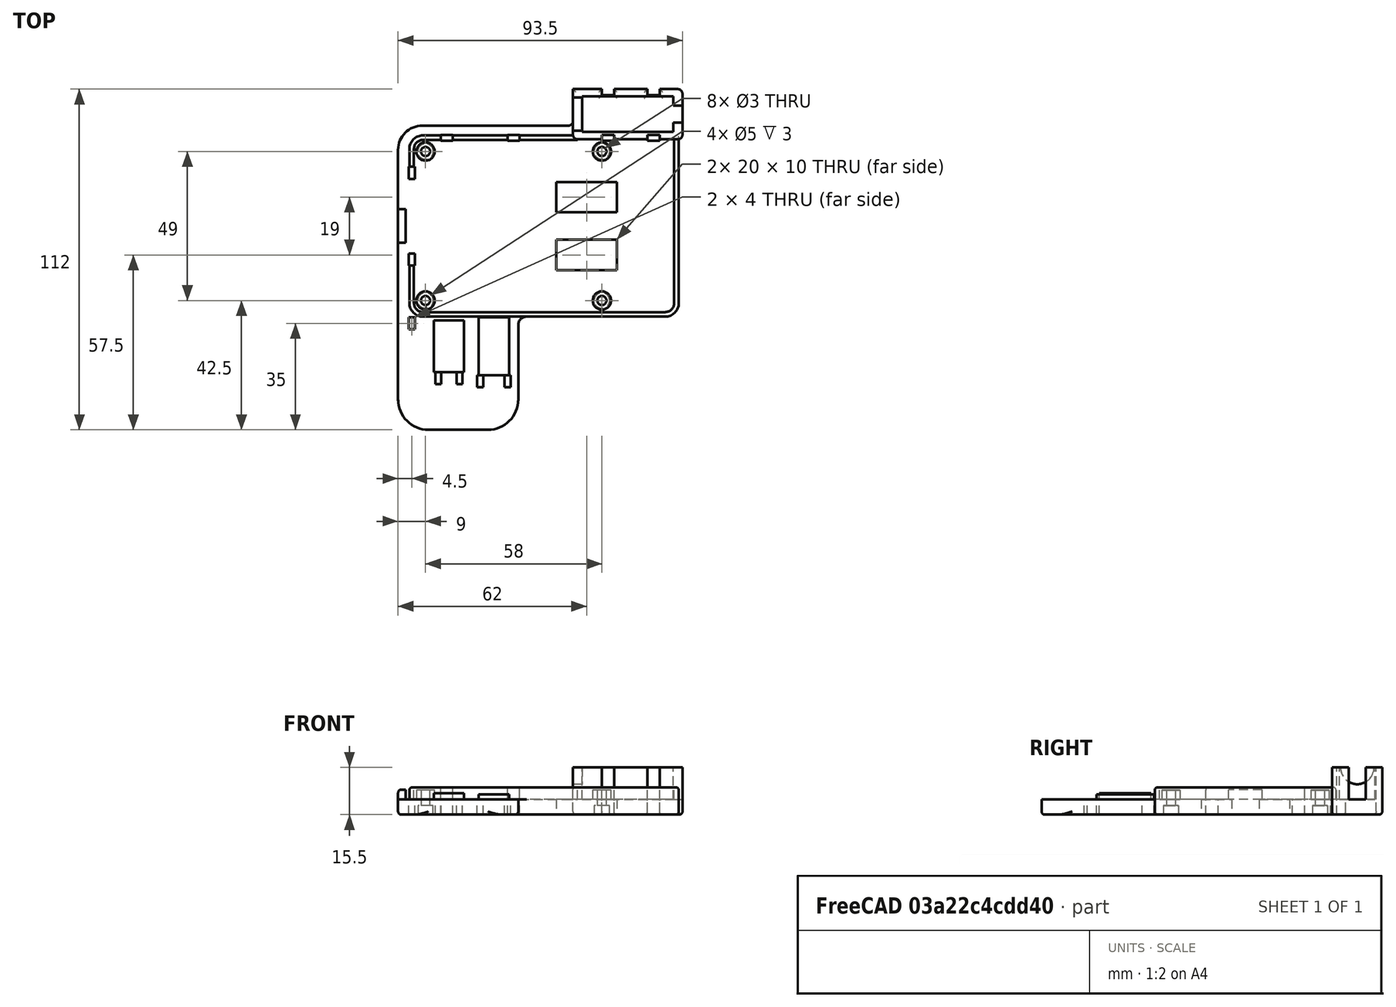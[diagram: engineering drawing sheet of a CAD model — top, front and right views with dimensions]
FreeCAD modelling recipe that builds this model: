
FCSTD DOCUMENT  (FreeCAD 0.18R4 (GitTag))
Label: v1.1raspberry_holster
License: All rights reserved
LicenseURL: http://en.wikipedia.org/wiki/All_rights_reserved
objects: Sketcher::SketchObject×12, PartDesign::Pad×7, PartDesign::Pocket×5, PartDesign::Fillet×3, Mesh::Feature×1, PartDesign::Body×1
note: 40 computed .brp shape members not serialized (recipe doc carries the construction recipe); baked Part::Feature solids carry a one-line shape summary decoded from their .brp

FEATURE [Mesh::Feature] Raspberry_Pi_4
  Placement = pos=(39,24.5,7.5) rot=(0,0,1;0rad)
FEATURE [Sketcher::SketchObject] Sketch  label="bottom_plane"
  MapMode = 5
  Support = -> [XY_Plane]
  sketch-geometry (71):
    g0: Circle CenterX=0 CenterY=49 CenterZ=0 NormalX=0 NormalY=0 NormalZ=1 AngleXU=0 Radius=1.5
    g1: Circle CenterX=58 CenterY=49 CenterZ=0 NormalX=0 NormalY=0 NormalZ=1 AngleXU=0 Radius=1.5
    g2: Circle CenterX=0 CenterY=0 CenterZ=0 NormalX=0 NormalY=0 NormalZ=1 AngleXU=0 Radius=1.5
    g3: Circle CenterX=58 CenterY=0 CenterZ=0 NormalX=0 NormalY=0 NormalZ=1 AngleXU=0 Radius=1.5
    g4: LineSegment StartX=84.5 StartY=68 StartZ=0 EndX=84.5 EndY=-5 EndZ=0
    g5: ArcOfCircle CenterX=83 CenterY=68 CenterZ=0 NormalX=0 NormalY=0 NormalZ=1 AngleXU=0 Radius=1.5 StartAngle=-9e-16 EndAngle=1.5708
    g6: LineSegment StartX=48.5 StartY=69.5 StartZ=0 EndX=48.5 EndY=59 EndZ=0
    g7: ArcOfCircle CenterX=47 CenterY=59 CenterZ=0 NormalX=0 NormalY=0 NormalZ=1 AngleXU=0 Radius=1.5 StartAngle=4.71239 EndAngle=6.28319
    g8: LineSegment StartX=47 StartY=57.5 StartZ=0 EndX=-1 EndY=57.5 EndZ=0
    g9: LineSegment StartX=-9 StartY=49.5 StartZ=0 EndX=-9 EndY=-41 EndZ=0
    g10: ArcOfCircle CenterX=-1 CenterY=49.5 CenterZ=0 NormalX=0 NormalY=0 NormalZ=1 AngleXU=0 Radius=8 StartAngle=1.5708 EndAngle=3.14159
    g11: LineSegment StartX=-7.5 StartY=-42.5 StartZ=0 EndX=29 EndY=-42.5 EndZ=0
    g12: ArcOfCircle CenterX=-7.5 CenterY=-41 CenterZ=0 NormalX=0 NormalY=0 NormalZ=1 AngleXU=0 Radius=1.5 StartAngle=3.14159 EndAngle=4.71239
    g13: ArcOfCircle CenterX=83 CenterY=-5 CenterZ=0 NormalX=0 NormalY=0 NormalZ=1 AngleXU=0 Radius=1.5 StartAngle=4.71239 EndAngle=6.28319
    g14: LineSegment StartX=32 StartY=-6.5 StartZ=0 EndX=83 EndY=-6.5 EndZ=0
    g15: LineSegment StartX=30.5 StartY=-8 StartZ=0 EndX=30.5 EndY=-41 EndZ=0
    g16: ArcOfCircle CenterX=32 CenterY=-8 CenterZ=0 NormalX=0 NormalY=0 NormalZ=1 AngleXU=0 Radius=1.5 StartAngle=1.5708 EndAngle=3.14159
    g17: ArcOfCircle CenterX=29 CenterY=-41 CenterZ=0 NormalX=0 NormalY=0 NormalZ=1 AngleXU=0 Radius=1.5 StartAngle=4.71239 EndAngle=6.28319
    g18: LineSegment StartX=58 StartY=52.5 StartZ=0 EndX=62 EndY=52.5 EndZ=0
    g19: LineSegment StartX=62 StartY=52.5 StartZ=0 EndX=62 EndY=54.5 EndZ=0
    g20: LineSegment StartX=62 StartY=54.5 StartZ=0 EndX=58 EndY=54.5 EndZ=0
    g21: LineSegment StartX=58 StartY=54.5 StartZ=0 EndX=58 EndY=52.5 EndZ=0
    g22: LineSegment StartX=73 StartY=54.5 StartZ=0 EndX=77 EndY=54.5 EndZ=0
    g23: LineSegment StartX=77 StartY=54.5 StartZ=0 EndX=77 EndY=52.5 EndZ=0
    g24: LineSegment StartX=77 StartY=52.5 StartZ=0 EndX=73 EndY=52.5 EndZ=0
    g25: LineSegment StartX=73 StartY=52.5 StartZ=0 EndX=73 EndY=54.5 EndZ=0
    g26: LineSegment StartX=48.5 StartY=69.5 StartZ=0 EndX=58 EndY=69.5 EndZ=0
    g27: LineSegment StartX=58 StartY=69.5 StartZ=0 EndX=58 EndY=67.5 EndZ=0
    g28: LineSegment StartX=58 StartY=67.5 StartZ=0 EndX=62 EndY=67.5 EndZ=0
    g29: LineSegment StartX=62 StartY=67.5 StartZ=0 EndX=62 EndY=69.5 EndZ=0
    g30: LineSegment StartX=62 StartY=69.5 StartZ=0 EndX=73 EndY=69.5 EndZ=0
    g31: LineSegment StartX=73 StartY=69.5 StartZ=0 EndX=73 EndY=67.5 EndZ=0
    g32: LineSegment StartX=73 StartY=67.5 StartZ=0 EndX=77 EndY=67.5 EndZ=0
    g33: LineSegment StartX=77 StartY=67.5 StartZ=0 EndX=77 EndY=69.5 EndZ=0
    g34: LineSegment StartX=77 StartY=69.5 StartZ=0 EndX=83 EndY=69.5 EndZ=0
    g35: LineSegment StartX=31 StartY=54.5 StartZ=0 EndX=27 EndY=54.5 EndZ=0
    g36: LineSegment StartX=27 StartY=54.5 StartZ=0 EndX=27 EndY=52.5 EndZ=0
    g37: LineSegment StartX=27 StartY=52.5 StartZ=0 EndX=31 EndY=52.5 EndZ=0
    g38: LineSegment StartX=31 StartY=52.5 StartZ=0 EndX=31 EndY=54.5 EndZ=0
    g39: LineSegment StartX=9 StartY=54.5 StartZ=0 EndX=5 EndY=54.5 EndZ=0
    g40: LineSegment StartX=5 StartY=54.5 StartZ=0 EndX=5 EndY=52.5 EndZ=0
    g41: LineSegment StartX=5 StartY=52.5 StartZ=0 EndX=9 EndY=52.5 EndZ=0
    g42: LineSegment StartX=9 StartY=52.5 StartZ=0 EndX=9 EndY=54.5 EndZ=0
    g43: LineSegment StartX=-5.5 StartY=44 StartZ=0 EndX=-3.5 EndY=44 EndZ=0
    g44: LineSegment StartX=-3.5 StartY=44 StartZ=0 EndX=-3.5 EndY=40 EndZ=0
    g45: LineSegment StartX=-3.5 StartY=40 StartZ=0 EndX=-5.5 EndY=40 EndZ=0
    g46: LineSegment StartX=-5.5 StartY=40 StartZ=0 EndX=-5.5 EndY=44 EndZ=0
    g47: LineSegment StartX=-5.5 StartY=15.5 StartZ=0 EndX=-3.5 EndY=15.5 EndZ=0
    g48: LineSegment StartX=-3.5 StartY=15.5 StartZ=0 EndX=-3.5 EndY=11.5 EndZ=0
    g49: LineSegment StartX=-3.5 StartY=11.5 StartZ=0 EndX=-5.5 EndY=11.5 EndZ=0
    g50: LineSegment StartX=-5.5 StartY=11.5 StartZ=0 EndX=-5.5 EndY=15.5 EndZ=0
    g51: LineSegment StartX=-5.5 StartY=-5.5 StartZ=0 EndX=-3.5 EndY=-5.5 EndZ=0
    g52: LineSegment StartX=-3.5 StartY=-5.5 StartZ=0 EndX=-3.5 EndY=-9.5 EndZ=0
    g53: LineSegment StartX=-3.5 StartY=-9.5 StartZ=0 EndX=-5.5 EndY=-9.5 EndZ=0
    g54: LineSegment StartX=-5.5 StartY=-9.5 StartZ=0 EndX=-5.5 EndY=-5.5 EndZ=0
    g55: LineSegment StartX=3.2 StartY=-23.5 StartZ=0 EndX=5.2 EndY=-23.5 EndZ=0
    g56: LineSegment StartX=5.2 StartY=-23.5 StartZ=0 EndX=5.2 EndY=-27.5 EndZ=0
    g57: LineSegment StartX=5.2 StartY=-27.5 StartZ=0 EndX=3.2 EndY=-27.5 EndZ=0
    g58: LineSegment StartX=3.2 StartY=-27.5 StartZ=0 EndX=3.2 EndY=-23.5 EndZ=0
    g59: LineSegment StartX=10.2 StartY=-23.5 StartZ=0 EndX=12.2 EndY=-23.5 EndZ=0
    g60: LineSegment StartX=12.2 StartY=-23.5 StartZ=0 EndX=12.2 EndY=-27.5 EndZ=0
    g61: LineSegment StartX=12.2 StartY=-27.5 StartZ=0 EndX=10.2 EndY=-27.5 EndZ=0
    g62: LineSegment StartX=10.2 StartY=-27.5 StartZ=0 EndX=10.2 EndY=-23.5 EndZ=0
    g63: LineSegment StartX=17 StartY=-24.5 StartZ=0 EndX=19 EndY=-24.5 EndZ=0
    g64: LineSegment StartX=19 StartY=-24.5 StartZ=0 EndX=19 EndY=-28.5 EndZ=0
    g65: LineSegment StartX=19 StartY=-28.5 StartZ=0 EndX=17 EndY=-28.5 EndZ=0
    g66: LineSegment StartX=17 StartY=-28.5 StartZ=0 EndX=17 EndY=-24.5 EndZ=0
    g67: LineSegment StartX=26 StartY=-24.5 StartZ=0 EndX=28 EndY=-24.5 EndZ=0
    g68: LineSegment StartX=28 StartY=-24.5 StartZ=0 EndX=28 EndY=-28.5 EndZ=0
    g69: LineSegment StartX=28 StartY=-28.5 StartZ=0 EndX=26 EndY=-28.5 EndZ=0
    g70: LineSegment StartX=26 StartY=-28.5 StartZ=0 EndX=26 EndY=-24.5 EndZ=0
  constraints (219):
    c: Coincident(g-1,g2)
    c: Vertical(g2,g0)
    c: Vertical(g1,g3)
    c: Horizontal(g1,g0)
    c: Horizontal(g3,g2)
    c: DistanceY(g2,g0) = 49
    c: DistanceX(g2,g3) = 58
    c: Radius(g2) = 1.5
    c: Equal(g2,g3)
    c: Equal(g3,g1)
    c: Equal(g1,g0)
    c: Vertical(g4)
    c: DistanceX(g3,g4) = 26.5
    c: Coincident(g5,g4)
    c: Vertical(g5,g5)
    c: Horizontal(g4,g5)
    c: Radius(g5) = 1.5
    c: Coincident(g6,g7)
    c: Vertical(g7,g7)
    c: Horizontal(g7,g6)
    c: Radius(g7) = 1.5
    c: Vertical(g6)
    c: DistanceX(g6,g4) = 36
    c: Coincident(g8,g7)
    c: Horizontal(g8)
    c: Vertical(g9)
    c: DistanceX(g9,g0) = 9
    c: DistanceY(g1,g7) = 8.5
    c: Coincident(g10,g8)
    c: Coincident(g9,g10)
    c: Vertical(g10,g8)
    c: Horizontal(g10,g9)
    c: Horizontal(g11)
    c: DistanceY(g11,g2) = 42.5
    c: Coincident(g11,g12)
    c: Coincident(g12,g9)
    c: Vertical(g12,g11)
    c: Horizontal(g9,g12)
    c: Radius(g12) = 1.5
    c: Coincident(g13,g4)
    c: Horizontal(g13,g4)
    c: Vertical(g13,g13)
    c: Radius(g13) = 1.5
    c: Coincident(g14,g13)
    c: Horizontal(g14)
    c: Coincident(g16,g14)
    c: Coincident(g16,g15)
    c: Vertical(g16,g14)
    c: Horizontal(g16,g15)
    c: DistanceY(g14,g3) = 6.5
    c: DistanceX(g2,g15) = 30.5
    c: Vertical(g15)
    c: Coincident(g17,g11)
    c: Coincident(g17,g15)
    c: Horizontal(g17,g15)
    c: Vertical(g11,g17)
    c: Radius(g17) = 1.5
    c: Radius(g16) = 1.5
    c: Coincident(g18,g19)
    c: Coincident(g19,g20)
    c: Coincident(g20,g21)
    c: Coincident(g21,g18)
    c: Horizontal(g18)
    c: Horizontal(g20)
    c: Vertical(g19)
    c: Vertical(g21)
    c: DistanceY(g18,g20) = 2
    c: DistanceX(g20,g19) = 4
    c: DistanceY(g1,g18) = 3.5
    c: Vertical(g1,g18)
    c: Coincident(g22,g23)
    c: Coincident(g23,g24)
    c: Coincident(g24,g25)
    c: Coincident(g25,g22)
    c: Horizontal(g22)
    c: Horizontal(g24)
    c: Vertical(g23)
    c: Vertical(g25)
    c: Horizontal(g22,g19)
    c: Horizontal(g24,g18)
    c: DistanceX(g22,g22) = 4
    c: DistanceX(g18,g24) = 15
    c: Coincident(g26,g27)
    c: Coincident(g27,g28)
    c: Coincident(g28,g29)
    c: Coincident(g29,g30)
    c: Coincident(g30,g31)
    c: Coincident(g31,g32)
    c: Coincident(g32,g33)
    c: Coincident(g33,g34)
    c: Coincident(g26,g6)
    c: Coincident(g34,g5)
    c: DistanceY(g1,g6) = 20.5
    c: Horizontal(g26)
    c: Horizontal(g30)
    c: Horizontal(g32)
    c: Horizontal(g34)
    c: Horizontal(g28)
    c: Vertical(g27)
    c: Vertical(g29)
    c: Vertical(g31)
    c: Vertical(g33)
    c: Horizontal(g26,g29)
    c: Horizontal(g30,g33)
    c: Horizontal(g31,g28)
    c: Vertical(g28,g19)
    c: Vertical(g20,g27)
    c: Vertical(g22,g31)
    c: Vertical(g22,g32)
    c: DistanceY(g28,g29) = 2
    c: Coincident(g35,g36)
    c: Coincident(g36,g37)
    c: Coincident(g38,g35)
    c: Horizontal(g35)
    c: Horizontal(g37)
    c: Vertical(g36)
    c: Vertical(g38)
    c: Coincident(g39,g40)
    c: Coincident(g40,g41)
    c: Coincident(g41,g42)
    c: Coincident(g42,g39)
    c: Horizontal(g39)
    c: Horizontal(g41)
    c: Vertical(g40)
    c: Vertical(g42)
    c: Coincident(g43,g44)
    c: Coincident(g44,g45)
    c: Coincident(g45,g46)
    c: Coincident(g46,g43)
    c: Horizontal(g43)
    c: Horizontal(g45)
    c: Vertical(g44)
    c: Vertical(g46)
    c: Coincident(g47,g48)
    c: Coincident(g48,g49)
    c: Coincident(g49,g50)
    c: Coincident(g50,g47)
    c: Horizontal(g47)
    c: Horizontal(g49)
    c: Vertical(g48)
    c: Vertical(g50)
    c: DistanceY(g1,g37) = 3.5
    c: DistanceX(g36,g37) = 4
    c: DistanceY(g37,g35) = 2
    c: DistanceX(g40,g41) = 4
    c: Horizontal(g41,g36)
    c: Horizontal(g39,g35)
    c: DistanceX(g37,g1) = 27
    c: DistanceX(g43,g0) = 3.5
    c: DistanceX(g43,g43) = 2
    c: DistanceY(g44,g43) = 4
    c: Vertical(g44,g47)
    c: Vertical(g47,g45)
    c: DistanceY(g49,g47) = 4
    c: DistanceY(g43,g0) = 5
    c: DistanceX(g0,g40) = 5
    c: DistanceY(g47,g44) = 24.5
    c: Coincident(g37,g38)
    c: Coincident(g51,g52)
    c: Coincident(g52,g53)
    c: Coincident(g53,g54)
    c: Coincident(g54,g51)
    c: Horizontal(g51)
    c: Horizontal(g53)
    c: Vertical(g52)
    c: Vertical(g54)
    c: Vertical(g51,g49)
    c: Vertical(g51,g48)
    c: DistanceY(g53,g51) = 4
    c: DistanceY(g51,g48) = 17
    c: Coincident(g55,g56)
    c: Coincident(g56,g57)
    c: Coincident(g57,g58)
    c: Coincident(g58,g55)
    c: Horizontal(g55)
    c: Horizontal(g57)
    c: Vertical(g56)
    c: Vertical(g58)
    c: Coincident(g59,g60)
    c: Coincident(g60,g61)
    c: Coincident(g61,g62)
    c: Coincident(g62,g59)
    c: Horizontal(g59)
    c: Horizontal(g61)
    c: Vertical(g60)
    c: Vertical(g62)
    c: Coincident(g63,g64)
    c: Coincident(g64,g65)
    c: Coincident(g65,g66)
    c: Coincident(g66,g63)
    c: Horizontal(g63)
    c: Horizontal(g65)
    c: Vertical(g64)
    c: Vertical(g66)
    c: Coincident(g67,g68)
    c: Coincident(g68,g69)
    c: Coincident(g69,g70)
    c: Coincident(g70,g67)
    c: Horizontal(g67)
    c: Horizontal(g69)
    c: Vertical(g68)
    c: Vertical(g70)
    c: DistanceX(g55,g55) = 2
    c: DistanceY(g56,g55) = 4
    c: Horizontal(g56,g61)
    c: Horizontal(g65,g69)
    c: Horizontal(g67,g63)
    c: Horizontal(g59,g55)
    c: DistanceX(g59,g59) = 2
    c: DistanceX(g63,g63) = 2
    c: DistanceX(g67,g67) = 2
    c: DistanceX(g56,g61) = 5
    c: DistanceX(g64,g69) = 7
    c: DistanceY(g65,g63) = 4
    c: DistanceY(g55,g2) = 23.5
    c: DistanceY(g63,g2) = 24.5
    c: DistanceX(g2,g55) = 5.2
    c: DistanceX(g2,g63) = 19
    c: Radius(g10) = 8
FEATURE [PartDesign::Pad] Pad  label="bottom_plane_pad"
  Length = 5
  Length2 = 100
  Profile = -> Sketch
  Type = 0
FEATURE [Sketcher::SketchObject] Sketch001  label="standoffs"
  ExternalGeometry = -> [Pad]
  MapMode = 5
  Placement = pos=(0,0,5) rot=(0,0,1;0rad)
  Support = -> [Pad]
  sketch-geometry (8):
    g0: Circle CenterX=0 CenterY=49 CenterZ=0 NormalX=0 NormalY=0 NormalZ=1 AngleXU=0 Radius=3
    g1: Circle CenterX=58 CenterY=49 CenterZ=0 NormalX=0 NormalY=0 NormalZ=1 AngleXU=0 Radius=3
    g2: Circle CenterX=58 CenterY=0 CenterZ=0 NormalX=0 NormalY=0 NormalZ=1 AngleXU=0 Radius=3
    g3: Circle CenterX=0 CenterY=0 CenterZ=0 NormalX=0 NormalY=0 NormalZ=1 AngleXU=0 Radius=3
    g4: Circle CenterX=58 CenterY=0 CenterZ=0 NormalX=0 NormalY=0 NormalZ=1 AngleXU=0 Radius=1.5
    g5: Circle CenterX=58 CenterY=49 CenterZ=0 NormalX=0 NormalY=0 NormalZ=1 AngleXU=0 Radius=1.5
    g6: Circle CenterX=0 CenterY=49 CenterZ=0 NormalX=0 NormalY=0 NormalZ=1 AngleXU=0 Radius=1.5
    g7: Circle CenterX=0 CenterY=0 CenterZ=0 NormalX=0 NormalY=0 NormalZ=1 AngleXU=0 Radius=1.5
  constraints (16):
    c: Coincident(g3,g-1)
    c: Coincident(g-5,g0)
    c: Coincident(g-6,g1)
    c: Coincident(g-3,g2)
    c: Equal(g2,g1)
    c: Equal(g1,g0)
    c: Equal(g0,g3)
    c: Radius(g1) = 3
    c: Coincident(g7,g3)
    c: Coincident(g2,g4)
    c: Coincident(g5,g1)
    c: Coincident(g6,g0)
    c: Equal(g5,g4)
    c: Equal(g4,g7)
    c: Equal(g7,g6)
    c: Equal(g6,g-5)
FEATURE [PartDesign::Pad] Pad001  label="standoffs_pad"
  BaseFeature = -> Pad
  Length = 3
  Length2 = 100
  Profile = -> Sketch001
  Type = 0
FEATURE [Sketcher::SketchObject] Sketch002  label="HDMI_holder"
  ExternalGeometry = -> [Pad001]
  MapMode = 5
  Placement = pos=(0,0,5) rot=(0,0,1;0rad)
  Support = -> [Pad001]
  sketch-geometry (31):
    g0: LineSegment StartX=84.5 StartY=54.5 StartZ=0 EndX=84.5 EndY=58.5 EndZ=0
    g1: LineSegment StartX=51.5 StartY=55.5 StartZ=0 EndX=81.5 EndY=55.5 EndZ=0
    g2: LineSegment StartX=81.5 StartY=55.5 StartZ=0 EndX=81.5 EndY=58.5 EndZ=0
    g3: LineSegment StartX=81.5 StartY=58.5 StartZ=0 EndX=84.5 EndY=58.5 EndZ=0
    g4: LineSegment StartX=51.5 StartY=55.5 StartZ=0 EndX=51.5 EndY=67.1 EndZ=0
    g5: LineSegment StartX=48.5 StartY=69.5 StartZ=0 EndX=48.5 EndY=54.5 EndZ=0
    g6: LineSegment StartX=51.5 StartY=67.1 StartZ=0 EndX=81.5 EndY=67.1 EndZ=0
    g7: LineSegment StartX=81.5 StartY=67.1 StartZ=0 EndX=81.5 EndY=64.1 EndZ=0
    g8: LineSegment StartX=81.5 StartY=64.1 StartZ=0 EndX=84.5 EndY=64.1 EndZ=0
    g9: LineSegment StartX=84.5 StartY=64.1 StartZ=0 EndX=84.5 EndY=68 EndZ=0
    g10: ArcOfCircle CenterX=83 CenterY=68 CenterZ=0 NormalX=0 NormalY=0 NormalZ=1 AngleXU=0 Radius=1.5 StartAngle=1.4e-15 EndAngle=1.5708
    g11: LineSegment StartX=83 StartY=69.5 StartZ=0 EndX=77 EndY=69.5 EndZ=0
    g12: LineSegment StartX=77 StartY=69.5 StartZ=0 EndX=77 EndY=67.5 EndZ=0
    g13: LineSegment StartX=77 StartY=67.5 StartZ=0 EndX=73 EndY=67.5 EndZ=0
    g14: LineSegment StartX=73 StartY=67.5 StartZ=0 EndX=73 EndY=69.5 EndZ=0
    g15: LineSegment StartX=73 StartY=69.5 StartZ=0 EndX=62 EndY=69.5 EndZ=0
    g16: LineSegment StartX=62 StartY=69.5 StartZ=0 EndX=62 EndY=67.5 EndZ=0
    g17: LineSegment StartX=62 StartY=67.5 StartZ=0 EndX=58 EndY=67.5 EndZ=0
    g18: LineSegment StartX=58 StartY=67.5 StartZ=0 EndX=58 EndY=69.5 EndZ=0
    g19: LineSegment StartX=58 StartY=69.5 StartZ=0 EndX=48.5 EndY=69.5 EndZ=0
    g20: ArcOfCircle CenterX=50 CenterY=54.5 CenterZ=0 NormalX=0 NormalY=0 NormalZ=1 AngleXU=0 Radius=1.5 StartAngle=3.14159 EndAngle=4.71239
    g21: LineSegment StartX=83 StartY=53 StartZ=0 EndX=77 EndY=53 EndZ=0
    g22: LineSegment StartX=77 StartY=53 StartZ=0 EndX=77 EndY=54.5 EndZ=0
    g23: LineSegment StartX=77 StartY=54.5 StartZ=0 EndX=73 EndY=54.5 EndZ=0
    g24: LineSegment StartX=73 StartY=54.5 StartZ=0 EndX=73 EndY=53 EndZ=0
    g25: LineSegment StartX=73 StartY=53 StartZ=0 EndX=62 EndY=53 EndZ=0
    g26: LineSegment StartX=62 StartY=53 StartZ=0 EndX=62 EndY=54.5 EndZ=0
    g27: LineSegment StartX=62 StartY=54.5 StartZ=0 EndX=58 EndY=54.5 EndZ=0
    g28: LineSegment StartX=58 StartY=54.5 StartZ=0 EndX=58 EndY=53 EndZ=0
    g29: LineSegment StartX=58 StartY=53 StartZ=0 EndX=50 EndY=53 EndZ=0
    g30: ArcOfCircle CenterX=83 CenterY=54.5 CenterZ=0 NormalX=0 NormalY=0 NormalZ=1 AngleXU=0 Radius=1.5 StartAngle=4.71239 EndAngle=6.28319
  constraints (84):
    c: Vertical(g0,g-6)
    c: Horizontal(g1)
    c: DistanceY(g20,g1) = 2.5
    c: Coincident(g0,g3)
    c: Coincident(g3,g2)
    c: Coincident(g2,g1)
    c: DistanceX(g2,g0) = 3
    c: Vertical(g0)
    c: Horizontal(g3)
    c: Vertical(g2)
    c: DistanceX(g1,g1) = 30
    c: DistanceY(g1,g2) = 3
    c: Coincident(g4,g6)
    c: Coincident(g1,g4)
    c: Coincident(g8,g9)
    c: Coincident(g7,g8)
    c: Coincident(g6,g7)
    c: Horizontal(g6)
    c: Vertical(g4)
    c: DistanceY(g1,g4) = 11.6
    c: Vertical(g7)
    c: Horizontal(g8)
    c: Vertical(g9)
    c: Vertical(g7,g2)
    c: DistanceY(g7,g6) = 3
    c: Coincident(g9,g-6)
    c: Coincident(g9,g10)
    c: Horizontal(g9,g10)
    c: Vertical(g10,g10)
    c: Radius(g10) = 1.5
    c: Coincident(g11,g12)
    c: Coincident(g12,g13)
    c: Coincident(g13,g14)
    c: Coincident(g14,g15)
    c: Coincident(g15,g16)
    c: Coincident(g16,g17)
    c: Coincident(g17,g18)
    c: Coincident(g18,g19)
    c: Coincident(g11,g10)
    c: Horizontal(g11)
    c: Vertical(g12)
    c: Coincident(g12,g-4)
    c: Coincident(g13,g-4)
    c: Coincident(g14,g-7)
    c: Coincident(g15,g-7)
    c: Coincident(g16,g-5)
    c: Coincident(g17,g-5)
    c: Coincident(g19,g-8)
    c: Horizontal(g19)
    c: Vertical(g18)
    c: Coincident(g5,g19)
    c: Coincident(g5,g20)
    c: Horizontal(g20,g5)
    c: Vertical(g20,g20)
    c: Radius(g20) = 1.5
    c: Vertical(g5)
    c: Coincident(g21,g22)
    c: Coincident(g22,g23)
    c: Coincident(g23,g24)
    c: Coincident(g24,g25)
    c: Coincident(g25,g26)
    c: Coincident(g26,g27)
    c: Coincident(g27,g28)
    c: Coincident(g28,g29)
    c: Coincident(g20,g29)
    c: Coincident(g27,g-12)
    c: Coincident(g26,g-11)
    c: Coincident(g23,g-10)
    c: Coincident(g22,g-9)
    c: Coincident(g30,g0)
    c: Coincident(g21,g30)
    c: Vertical(g30,g21)
    c: Horizontal(g30,g0)
    c: Radius(g30) = 1.5
    c: DistanceY(g-3,g28) = 4
    c: Horizontal(g29)
    c: Horizontal(g25)
    c: Horizontal(g21)
    c: Horizontal(g21,g24)
    c: Horizontal(g25,g28)
    c: Vertical(g28)
    c: Vertical(g26)
    c: Vertical(g24)
    c: Vertical(g22)
FEATURE [PartDesign::Pad] Pad002  label="HDMI_holder_pad"
  BaseFeature = -> Pad001
  Length = 10.5
  Length2 = 100
  Profile = -> Sketch002
  Type = 0
FEATURE [Sketcher::SketchObject] Sketch003  label="HDMI_wire_hole"
  ExternalGeometry = -> [Pad002]
  MapMode = 5
  Placement = pos=(48.5,0,0) rot=(0.57735,-0.57735,-0.57735;2.0944rad)
  Support = -> [Pad002]
  sketch-geometry (1):
    g0: Circle CenterX=-61.3 CenterY=15.5 CenterZ=0 NormalX=0 NormalY=0 NormalZ=1 AngleXU=0 Radius=5.5
  constraints (1):
    c: Radius(g0) = 5.5
FEATURE [PartDesign::Pocket] Pocket  label="Pocket_HDMI_wire_hole"
  BaseFeature = -> Pad002
  Length = 5
  Length2 = 100
  Profile = -> Sketch003
  Type = 0
FEATURE [Sketcher::SketchObject] Sketch004  label="SDcard_holder"
  ExternalGeometry = -> [Pocket]
  MapMode = 5
  Placement = pos=(0,0,5) rot=(0,0,1;0rad)
  Support = -> [Pocket]
  sketch-geometry (4):
    g0: LineSegment StartX=-9 StartY=30 StartZ=0 EndX=-6.5 EndY=30 EndZ=0
    g1: LineSegment StartX=-6.5 StartY=30 StartZ=0 EndX=-6.5 EndY=19 EndZ=0
    g2: LineSegment StartX=-6.5 StartY=19 StartZ=0 EndX=-9 EndY=19 EndZ=0
    g3: LineSegment StartX=-9 StartY=19 StartZ=0 EndX=-9 EndY=30 EndZ=0
  constraints (12):
    c: Coincident(g0,g1)
    c: Coincident(g1,g2)
    c: Coincident(g2,g3)
    c: Coincident(g3,g0)
    c: Horizontal(g0)
    c: Horizontal(g2)
    c: Vertical(g1)
    c: Vertical(g3)
    c: DistanceY(g-1,g1) = 19
    c: DistanceY(g0,g-4) = 19
    c: Vertical(g0,g-5)
    c: DistanceX(g1,g-1) = 6.5
FEATURE [PartDesign::Pad] Pad003  label="SDcard_holder_pad"
  BaseFeature = -> Pocket
  Length = 3.2
  Length2 = 100
  Profile = -> Sketch004
  Type = 0
FEATURE [Sketcher::SketchObject] Sketch005  label="typeC_support"
  ExternalGeometry = -> [Pad003]
  MapMode = 5
  Placement = pos=(0,0,5) rot=(0,0,1;0rad)
  Support = -> [Pad003]
  sketch-geometry (4):
    g0: LineSegment StartX=2.7 StartY=-6.5 StartZ=0 EndX=12.7 EndY=-6.5 EndZ=0
    g1: LineSegment StartX=12.7 StartY=-6.5 StartZ=0 EndX=12.7 EndY=-23.5 EndZ=0
    g2: LineSegment StartX=12.7 StartY=-23.5 StartZ=0 EndX=2.7 EndY=-23.5 EndZ=0
    g3: LineSegment StartX=2.7 StartY=-23.5 StartZ=0 EndX=2.7 EndY=-6.5 EndZ=0
  constraints (12):
    c: Coincident(g0,g1)
    c: Coincident(g1,g2)
    c: Coincident(g2,g3)
    c: Coincident(g3,g0)
    c: Horizontal(g0)
    c: Horizontal(g2)
    c: Vertical(g1)
    c: Vertical(g3)
    c: DistanceX(g0,g0) = 10
    c: DistanceY(g1,g1) = 17
    c: Horizontal(g2,g-4)
    c: DistanceX(g-1,g0) = 2.7
FEATURE [PartDesign::Pad] Pad004  label="typeC_support_pad"
  BaseFeature = -> Pad003
  Length = 2
  Length2 = 100
  Profile = -> Sketch005
  Type = 0
FEATURE [Sketcher::SketchObject] Sketch006  label="microHDMI_support"
  ExternalGeometry = -> [Pad004]
  MapMode = 5
  Placement = pos=(0,0,5) rot=(0,0,1;0rad)
  Support = -> [Pad004]
  sketch-geometry (4):
    g0: LineSegment StartX=17.5 StartY=-5.5 StartZ=0 EndX=27.5 EndY=-5.5 EndZ=0
    g1: LineSegment StartX=27.5 StartY=-5.5 StartZ=0 EndX=27.5 EndY=-24.5 EndZ=0
    g2: LineSegment StartX=27.5 StartY=-24.5 StartZ=0 EndX=17.5 EndY=-24.5 EndZ=0
    g3: LineSegment StartX=17.5 StartY=-24.5 StartZ=0 EndX=17.5 EndY=-5.5 EndZ=0
  constraints (12):
    c: Coincident(g0,g1)
    c: Coincident(g1,g2)
    c: Coincident(g2,g3)
    c: Coincident(g3,g0)
    c: Horizontal(g0)
    c: Horizontal(g2)
    c: Vertical(g1)
    c: Vertical(g3)
    c: DistanceX(g0,g0) = 10
    c: DistanceY(g1,g1) = 19
    c: Horizontal(g2,g-4)
    c: DistanceX(g-1,g0) = 17.5
FEATURE [PartDesign::Pad] Pad005  label="microHDMI_support_pad"
  BaseFeature = -> Pad004
  Length = 1.7
  Length2 = 100
  Profile = -> Sketch006
  Type = 0
FEATURE [Sketcher::SketchObject] Sketch007  label="dust_cover"
  ExternalGeometry = -> [Pad005]
  MapMode = 5
  Placement = pos=(0,0,5) rot=(0,0,1;0rad)
  Support = -> [Pad005]
  sketch-geometry (30):
    g0: LineSegment StartX=81.8 StartY=53 StartZ=0 EndX=81.8 EndY=-0.8 EndZ=0
    g1: LineSegment StartX=78.8 StartY=-3.8 StartZ=0 EndX=-0.8 EndY=-3.8 EndZ=0
    g2: LineSegment StartX=-3.8 StartY=49.8 StartZ=0 EndX=-3.8 EndY=44 EndZ=0
    g3: LineSegment StartX=-3.8 StartY=11.5 StartZ=0 EndX=-3.8 EndY=-0.8 EndZ=0
    g4: LineSegment StartX=-3.8 StartY=11.5 StartZ=0 EndX=-5.3 EndY=11.5 EndZ=0
    g5: ArcOfCircle CenterX=-0.8 CenterY=-0.8 CenterZ=0 NormalX=0 NormalY=0 NormalZ=1 AngleXU=0 Radius=3 StartAngle=3.14159 EndAngle=4.71239
    g6: ArcOfCircle CenterX=78.8 CenterY=-0.8 CenterZ=0 NormalX=0 NormalY=0 NormalZ=1 AngleXU=0 Radius=3 StartAngle=4.71239 EndAngle=6.28319
    g7: LineSegment StartX=81.8 StartY=53 StartZ=0 EndX=83 EndY=53 EndZ=0
    g8: LineSegment StartX=83.3 StartY=53.0303 StartZ=0 EndX=83.3 EndY=-0.8 EndZ=0
    g9: ArcOfCircle CenterX=83 CenterY=54.5 CenterZ=0 NormalX=0 NormalY=0 NormalZ=1 AngleXU=0 Radius=1.5 StartAngle=4.71239 EndAngle=4.91375
    g10: ArcOfCircle CenterX=78.8 CenterY=-0.8 CenterZ=0 NormalX=0 NormalY=0 NormalZ=1 AngleXU=0 Radius=4.5 StartAngle=4.71239 EndAngle=6.28319
    g11: LineSegment StartX=-0.8 StartY=-5.3 StartZ=0 EndX=78.8 EndY=-5.3 EndZ=0
    g12: ArcOfCircle CenterX=-0.8 CenterY=-0.8 CenterZ=0 NormalX=0 NormalY=0 NormalZ=1 AngleXU=0 Radius=4.5 StartAngle=3.14159 EndAngle=4.71239
    g13: LineSegment StartX=-5.3 StartY=-0.8 StartZ=0 EndX=-5.3 EndY=11.5 EndZ=0
    g14: LineSegment StartX=5 StartY=54.3 StartZ=0 EndX=5 EndY=52.8 EndZ=0
    g15: LineSegment StartX=5 StartY=54.3 StartZ=0 EndX=-0.8 EndY=54.3 EndZ=0
    g16: ArcOfCircle CenterX=-0.8 CenterY=49.8 CenterZ=0 NormalX=0 NormalY=0 NormalZ=1 AngleXU=0 Radius=4.5 StartAngle=1.5708 EndAngle=3.14159
    g17: LineSegment StartX=-3.8 StartY=44 StartZ=0 EndX=-5.3 EndY=44 EndZ=0
    g18: LineSegment StartX=-5.3 StartY=49.8 StartZ=0 EndX=-5.3 EndY=44 EndZ=0
    g19: LineSegment StartX=9 StartY=54.3 StartZ=0 EndX=27 EndY=54.3 EndZ=0
    g20: LineSegment StartX=27 StartY=54.3 StartZ=0 EndX=27 EndY=52.8 EndZ=0
    g21: LineSegment StartX=27 StartY=52.8 StartZ=0 EndX=9 EndY=52.8 EndZ=0
    g22: LineSegment StartX=9 StartY=52.8 StartZ=0 EndX=9 EndY=54.3 EndZ=0
    g23: LineSegment StartX=31 StartY=54.3 StartZ=0 EndX=31 EndY=52.8 EndZ=0
    g24: LineSegment StartX=31 StartY=52.8 StartZ=0 EndX=50 EndY=52.8 EndZ=0
    g25: LineSegment StartX=31 StartY=54.3 StartZ=0 EndX=48.5134 EndY=54.3 EndZ=0
    g26: LineSegment StartX=-0.8 StartY=52.8 StartZ=0 EndX=5 EndY=52.8 EndZ=0
    g27: LineSegment StartX=50 StartY=53 StartZ=0 EndX=50 EndY=52.8 EndZ=0
    g28: ArcOfCircle CenterX=50 CenterY=54.5 CenterZ=0 NormalX=0 NormalY=0 NormalZ=1 AngleXU=0 Radius=1.5 StartAngle=3.27532 EndAngle=4.71239
    g29: ArcOfCircle CenterX=-0.8 CenterY=49.8 CenterZ=0 NormalX=0 NormalY=0 NormalZ=1 AngleXU=0 Radius=3 StartAngle=1.5708 EndAngle=3.14159
  constraints (91):
    c: Vertical(g0)
    c: Horizontal(g1)
    c: Vertical(g3)
    c: Vertical(g2)
    c: DistanceX(g-3,g0) = 23.8
    c: DistanceY(g1,g-6) = 3.8
    c: Coincident(g4,g3)
    c: Horizontal(g3,g-7)
    c: Coincident(g5,g3)
    c: Coincident(g5,g1)
    c: Coincident(g6,g0)
    c: Coincident(g6,g1)
    c: Coincident(g7,g0)
    c: Horizontal(g7)
    c: Coincident(g7,g9)
    c: Coincident(g7,g-8)
    c: Vertical(g8)
    c: Coincident(g10,g8)
    c: Coincident(g10,g6)
    c: Coincident(g11,g10)
    c: Horizontal(g11)
    c: Coincident(g11,g12)
    c: Coincident(g12,g5)
    c: Coincident(g9,g-8)
    c: Coincident(g8,g9)
    c: DistanceX(g0,g8) = 1.5
    c: Coincident(g4,g13)
    c: Coincident(g12,g13)
    c: Vertical(g13)
    c: Horizontal(g4)
    c: Vertical(g14,g-9)
    c: Coincident(g14,g15)
    c: Vertical(g14)
    c: Horizontal(g15)
    c: Coincident(g15,g16)
    c: DistanceY(g26,g15) = 1.5
    c: Horizontal(g2,g-10)
    c: Coincident(g17,g2)
    c: Coincident(g17,g18)
    c: Coincident(g18,g16)
    c: Vertical(g18)
    c: Horizontal(g17)
    c: Coincident(g19,g20)
    c: Coincident(g20,g21)
    c: Coincident(g21,g22)
    c: Coincident(g22,g19)
    c: Horizontal(g19)
    c: Horizontal(g21)
    c: Vertical(g20)
    c: Vertical(g22)
    c: Vertical(g21,g-9)
    c: Vertical(g20,g-11)
    c: Horizontal(g21,g14)
    c: Horizontal(g19,g14)
    c: Coincident(g23,g24)
    c: Coincident(g23,g25)
    c: Vertical(g23)
    c: Vertical(g23,g-11)
    c: Horizontal(g23,g20)
    c: Horizontal(g23,g19)
    c: Horizontal(g24)
    c: Horizontal(g25)
    c: Coincident(g14,g26)
    c: Horizontal(g26)
    c: Coincident(g24,g27)
    c: Coincident(g27,g-12)
    c: Vertical(g27)
    c: Coincident(g25,g28)
    c: Coincident(g28,g27)
    c: Coincident(g28,g-12)
    c: Radius(g6) = 3
    c: Vertical(g10,g1)
    c: Vertical(g1,g6)
    c: Horizontal(g0,g6)
    c: Horizontal(g6,g8)
    c: Radius(g5) = 3
    c: Horizontal(g5,g3)
    c: Horizontal(g3,g12)
    c: Vertical(g11,g1)
    c: Vertical(g1,g5)
    c: DistanceX(g3,g-1) = 3.8
    c: Vertical(g26,g15)
    c: Horizontal(g2,g16)
    c: Coincident(g29,g26)
    c: Coincident(g29,g2)
    c: Coincident(g16,g29)
    c: Radius(g29) = 3
    c: Horizontal(g16,g2)
    c: Vertical(g16,g26)
    c: DistanceY(g-4,g26) = 3.8
    c: DistanceX(g2,g-4) = 3.8
FEATURE [PartDesign::Pad] Pad006  label="dust_cover_pad"
  BaseFeature = -> Pad005
  Length = 4
  Length2 = 100
  Profile = -> Sketch007
  Type = 0
FEATURE [Sketcher::SketchObject] Sketch008  label="top edge trim"
  ExternalGeometry = -> [Pad006]
  MapMode = 5
  Placement = pos=(0,0,5) rot=(0,0,1;0rad)
  Support = -> [Pad006]
  sketch-geometry (7):
    g0: ArcOfCircle CenterX=83 CenterY=54.5 CenterZ=0 NormalX=0 NormalY=0 NormalZ=1 AngleXU=0 Radius=1.5 StartAngle=4.91375 EndAngle=6.28319
    g1: LineSegment StartX=84.5 StartY=54.5 StartZ=0 EndX=84.5 EndY=-8 EndZ=0
    g2: LineSegment StartX=84.5 StartY=-8 StartZ=0 EndX=30.5 EndY=-8 EndZ=0
    g3: ArcOfCircle CenterX=33.2 CenterY=-8 CenterZ=0 NormalX=0 NormalY=0 NormalZ=1 AngleXU=0 Radius=2.7 StartAngle=1.5708 EndAngle=3.14159
    g4: LineSegment StartX=33.2 StartY=-5.3 StartZ=0 EndX=78.8 EndY=-5.3 EndZ=0
    g5: ArcOfCircle CenterX=78.8 CenterY=-0.8 CenterZ=0 NormalX=0 NormalY=0 NormalZ=1 AngleXU=0 Radius=4.5 StartAngle=4.71239 EndAngle=6.28319
    g6: LineSegment StartX=83.3 StartY=-0.8 StartZ=0 EndX=83.3 EndY=53.0303 EndZ=0
  constraints (19):
    c: Coincident(g0,g-7)
    c: Coincident(g0,g-3)
    c: Horizontal(g0,g0)
    c: Vertical(g1)
    c: Horizontal(g2)
    c: Coincident(g2,g1)
    c: Coincident(g1,g0)
    c: Coincident(g2,g-6)
    c: Coincident(g3,g2)
    c: Horizontal(g2,g3)
    c: Vertical(g3,g3)
    c: Horizontal(g3,g-5)
    c: Coincident(g4,g3)
    c: Coincident(g4,g-5)
    c: Coincident(g5,g4)
    c: Coincident(g5,g-4)
    c: Vertical(g4,g5)
    c: Coincident(g6,g5)
    c: Coincident(g6,g0)
FEATURE [PartDesign::Pocket] Pocket001  label="top edge trim pocket"
  BaseFeature = -> Pad006
  Length = 5
  Length2 = 100
  Profile = -> Sketch008
  Type = 0
FEATURE [Sketcher::SketchObject] Sketch009  label="belt clip guide"
  ExternalGeometry = -> [Pocket001]
  MapMode = 5
  Placement = pos=(0,0,5) rot=(0,0,1;0rad)
  Support = -> [Pocket001]
  sketch-geometry (8):
    g0: LineSegment StartX=63 StartY=39 StartZ=0 EndX=43 EndY=39 EndZ=0
    g1: LineSegment StartX=43 StartY=39 StartZ=0 EndX=43 EndY=29 EndZ=0
    g2: LineSegment StartX=43 StartY=29 StartZ=0 EndX=63 EndY=29 EndZ=0
    g3: LineSegment StartX=63 StartY=29 StartZ=0 EndX=63 EndY=39 EndZ=0
    g4: LineSegment StartX=63 StartY=20 StartZ=0 EndX=43 EndY=20 EndZ=0
    g5: LineSegment StartX=43 StartY=20 StartZ=0 EndX=43 EndY=10 EndZ=0
    g6: LineSegment StartX=43 StartY=10 StartZ=0 EndX=63 EndY=10 EndZ=0
    g7: LineSegment StartX=63 StartY=10 StartZ=0 EndX=63 EndY=20 EndZ=0
  constraints (24):
    c: Coincident(g0,g1)
    c: Coincident(g1,g2)
    c: Coincident(g2,g3)
    c: Coincident(g3,g0)
    c: Horizontal(g0)
    c: Horizontal(g2)
    c: Vertical(g1)
    c: Vertical(g3)
    c: Coincident(g4,g5)
    c: Coincident(g5,g6)
    c: Coincident(g6,g7)
    c: Coincident(g7,g4)
    c: Horizontal(g4)
    c: Horizontal(g6)
    c: Vertical(g5)
    c: Vertical(g7)
    c: Vertical(g4,g1)
    c: Vertical(g4,g2)
    c: DistanceY(g6,g4) = 10
    c: DistanceY(g2,g0) = 10
    c: DistanceX(g-3,g0) = 5
    c: DistanceX(g5,g6) = 20
    c: DistanceY(g-4,g6) = 10
    c: DistanceY(g0,g-3) = 10
FEATURE [PartDesign::Pocket] Pocket002  label="belt clip guide pocket"
  BaseFeature = -> Pocket001
  Length = 5
  Length2 = 100
  Profile = -> Sketch009
  Type = 0
FEATURE [PartDesign::Fillet] Fillet  label="underside fillet"
  Base = -> Pocket002 [Edge12,Edge3,Edge9,Edge13,Edge15,Edge17,Edge21,Edge19,Edge25,Edge23]
  BaseFeature = -> Pocket002
  Radius = 1
FEATURE [PartDesign::Fillet] Fillet001  label="SDcard fillet"
  Base = -> Fillet [Edge530]
  BaseFeature = -> Fillet
  Radius = 1
FEATURE [PartDesign::Fillet] Fillet002  label="dust cover fillet"
  Base = -> Fillet001 [Edge184,Edge178,Edge152,Edge138]
  BaseFeature = -> Fillet001
  Radius = 1
FEATURE [Sketcher::SketchObject] Sketch010  label="Wire quide trim"
  ExternalGeometry = -> [Fillet002]
  MapMode = 5
  Placement = pos=(0,0,5) rot=(0,0,1;0rad)
  Support = -> [Fillet002]
  sketch-geometry (6):
    g0: ArcOfCircle CenterX=1 CenterY=-32.5 CenterZ=0 NormalX=0 NormalY=0 NormalZ=1 AngleXU=0 Radius=10 StartAngle=3.14159 EndAngle=4.71239
    g1: ArcOfCircle CenterX=20.5 CenterY=-32.5 CenterZ=0 NormalX=0 NormalY=0 NormalZ=1 AngleXU=0 Radius=10 StartAngle=4.71239 EndAngle=6.28319
    g2: LineSegment StartX=1 StartY=-42.5 StartZ=0 EndX=20.5 EndY=-42.5 EndZ=0
    g3: LineSegment StartX=-9 StartY=-32.5 StartZ=0 EndX=-9 EndY=-43.5 EndZ=0
    g4: LineSegment StartX=-9 StartY=-43.5 StartZ=0 EndX=30.5 EndY=-43.5 EndZ=0
    g5: LineSegment StartX=30.5 StartY=-43.5 StartZ=0 EndX=30.5 EndY=-32.5 EndZ=0
  constraints (20):
    c: Coincident(g5,g1)
    c: Coincident(g5,g4)
    c: Coincident(g4,g3)
    c: Coincident(g3,g0)
    c: Coincident(g0,g2)
    c: Coincident(g2,g1)
    c: Equal(g1,g0)
    c: Radius(g1) = 10
    c: Horizontal(g2)
    c: Horizontal(g1,g1)
    c: Horizontal(g1,g0)
    c: Horizontal(g0,g0)
    c: Vertical(g3)
    c: Vertical(g5)
    c: Horizontal(g4)
    c: Vertical(g-5,g1)
    c: Vertical(g-4,g0)
    c: Horizontal(g0,g-3)
    c: DistanceY(g3,g0) = 1
    c: Vertical(g0,g0)
FEATURE [PartDesign::Pocket] Pocket003  label="wire quide trim pocket"
  BaseFeature = -> Fillet002
  Length = 5
  Length2 = 100
  Profile = -> Sketch010
  Type = 0
FEATURE [Sketcher::SketchObject] Sketch011  label="screw head space"
  ExternalGeometry = -> [Pocket003]
  MapMode = 5
  Placement = pos=(0,0,0) rot=(1,0,0;3.14159rad)
  Support = -> [Pocket003]
  sketch-geometry (4):
    g0: Circle CenterX=0 CenterY=0 CenterZ=0 NormalX=0 NormalY=0 NormalZ=1 AngleXU=0 Radius=2.5
    g1: Circle CenterX=58 CenterY=0 CenterZ=0 NormalX=0 NormalY=0 NormalZ=1 AngleXU=0 Radius=2.5
    g2: Circle CenterX=58 CenterY=-49 CenterZ=0 NormalX=0 NormalY=0 NormalZ=1 AngleXU=0 Radius=2.5
    g3: Circle CenterX=0 CenterY=-49 CenterZ=0 NormalX=0 NormalY=0 NormalZ=1 AngleXU=0 Radius=2.5
  constraints (8):
    c: Coincident(g3,g-5)
    c: Coincident(g-1,g0)
    c: Coincident(g1,g-3)
    c: Coincident(g2,g-6)
    c: Equal(g2,g1)
    c: Equal(g1,g0)
    c: Equal(g0,g3)
    c: Radius(g1) = 2.5
FEATURE [PartDesign::Pocket] Pocket004  label="screw head dent"
  BaseFeature = -> Pocket003
  Length = 3
  Length2 = 100
  Profile = -> Sketch011
  Type = 0
FEATURE [PartDesign::Body] Body  label="raspberry holster"
  Group = -> [Sketch,Pad,Sketch001,Pad001,Sketch002,Pad002,Sketch003,Pocket,Sketch004,Pad003,Sketch005,Pad004,Sketch006,Pad005,Sketch007,Pad006,Sketch008,Pocket001,Sketch009,Pocket002,Fillet,Fillet001,Fillet002,Sketch010,Pocket003,Sketch011,Pocket004]
  Origin = -> Origin
  Tip = -> Pocket004
